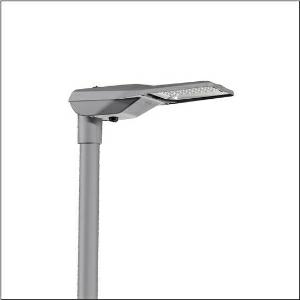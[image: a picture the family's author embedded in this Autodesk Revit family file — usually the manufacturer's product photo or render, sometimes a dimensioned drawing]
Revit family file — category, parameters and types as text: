
# Revit family: streetlight_sl_21_mini___st0_8a_5xe2c33t08hb_2b08
name_source: partatom
category: Lighting Fixtures
units: mm (PartAtom-declared; Revit-internal decimal feet)

## family parameters
Cut with Voids When Loaded = No
Host = Face
Light Source = No
Part Type = Normal
Room Calculation Point = No
Round Connector Dimension = Use Diameter
Shared = No

## types (1)
- --- (1 x LED, 9040 lm, 66 W, 3000K)
    Apparent Load = 66 VA
    CIE Flux Codes = 38 75 97 100 100
    Color Rendering = 70
    Color Temperature = 3000K
    Default Elevation = 1800 mm
    Description = Streetlight SL 21 mini, mast luminaire, primary light control with lens, of PMMA, primary optical cover: cover, of toughened safety glass, transparent, light distribution: ST0.8a, light emission: direct distribution, primary light characteristic: asymmetric, installation type: side-entry, post-top, LED, High Power LED, rated luminous flux: 9.040lm, luminous efficacy: 137lm/W, light colour: 730, colour temperature: 3000K, control gear: D4i, control: overheat protection, constant luminous flux control, time-dependent luminous flux control, flexible luminous flux parameterisation, pre-setting: logarithmic dimming characteristic, mains connection: 220..240V, AC, 50/60Hz, start of lifetime: 66W, end of service life: 69W, reduction: 30W, luminaire housing, of diecast aluminium, powder-coated, SITECO metallic grey (DB 702S), corrosivity category C5 high according to DIN EN ISO 12944, please order mast flange separately, inclination adjustable: 0°, 5°, 10°, 15°, sealing non-destructively replaceable, multi-level sealing system, length: 628mm, width: 235mm, height: 110mm, mast flange for spigot size: 42mm (side-entry): 5XC10008XM4, 60/48mm (side-entry/post-top): 5XC10108XM2, 76/60mm (side-entry/post-top): 5XC10108XM1, mounting height: 4..8m, Smart Interface below and above, protection rating (complete): IP66, insulation class (complete): insulation class II (safety insulation), certification: CE, ENEC, ENEC+, VDE, impact resistance: IK10, permissible operating ambient temperature for outdoor applications: -40..+50°C, standard-compliant lighting for roads and squares, packaging unit: 1 piece

Light Distribution: ST0.8a
    Height = 110 mm
    Lamp = 1 x LED
    Lamp Light Flux = 9040 lm
    Lamp Power = 66 W
    Lamp count = 1
    Length = 625 mm
    Luminous efficacy = 137 lm/W
    Manufacturer = Siteco
    ModVariant = No
    Model = 5XE2C33T08HB
    Number of Poles = 1
    OnlyDefault = Yes
    Power Factor = 1
    Product Name = Streetlight SL 21 mini | ST0.8a
    Product group = mast luminaire | pylon top
    ProductGroupID = 6100
    Protection Class = Protection class II
    Protection Degree = IP 66
    RLX_Detail_Level = 1
    RLX_Emergency_Light_Flux = 0 lm
    RLX_Emergency_Type = 0
    RLX_Emergency_Type_DB = No
    RlxData = <blob elided: 26389 chars, md5=0974827b>
    Socket = socket
    Standby Power = 0 W
    System Light Flux = 9040 lm
    System Power = 66 W
    Type Comments = factory setting: luminous flux: 100 % | dim-lin: 254 | 670 mA
    Type Image = l_1003514.jpg
    URL = http://relux.com
    VarID = @adj_182771
    Voltage = 0 V
    Weight = 0.00 kg
    Width = 234 mm

## geometry (parser evidence)
native form markers: Blend x4, Sweep x9
no freeform markers — native parametric forms only
